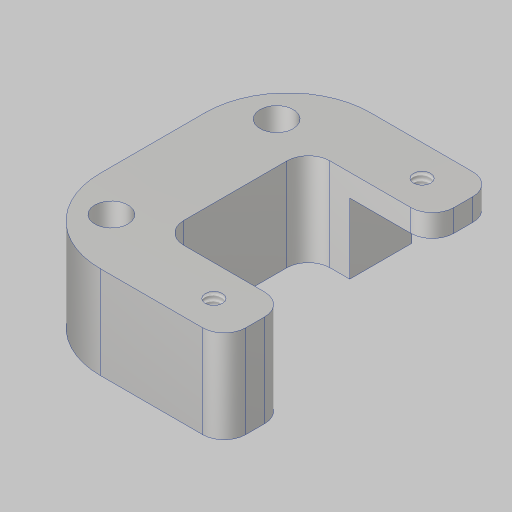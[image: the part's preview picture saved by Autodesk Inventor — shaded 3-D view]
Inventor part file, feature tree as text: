
AUTODESK INVENTOR PART (.ipt)
format: ipt  version: 2023.5 (Build 275446000, 446)  size: 196,096 bytes
history: native  units: in
note: dims shown in document units (in); Inventor stores cm internally (conversion verified against a paired STEP export)
features: sketch x6, extrude x4, projected_geometry x3, hole x2, fillet x2
ambient origin geometry x8: Origin, YZ Plane, XZ Plane, XY Plane, X Axis, Y Axis, Z Axis, Center Point
bodies: Solid1 (feature_tree)
feature tree (17):
  extrude  "Extrusion1"  Depth=1.2598in
  hole  "Hole1"  [1 undecoded]
  extrude  "Extrusion2"  Depth=0.25in
  extrude  "Extrusion3"  Depth=0.75in
  hole  "Hole3"  [1 undecoded]
  fillet  "Fillet1"  Radius=0.25in
  fillet  "Fillet2"  Radius=1.0in
  extrude  "Extrusion4"  Depth=0.5in
  sketch  "Sketch1"  dims[d1=1.2598in d2=0.31in]
  sketch  "Sketch2"  dims[d4=0.25in d5=0.375in]
  sketch  "Sketch4"  dims[d6=1.25in d7=0.0in d8=0.25in]
  sketch  "Sketch5"  dims[d9=0.104in d10=0.276in d11=0.375in d12=0.25in d13=0.5635in d14=1.0in d15=0.8108in d25=0.75in]
  sketch  "Sketch6"  dims[d26=1.5in d27=0.0in d28=1.5in d29=0.0in d30=0.25in d31=1.0in]
  sketch  "Sketch7"  dims[d32=0.201in d33=0.75in d34=0.375in d35=0.25in d36=0.5635in d37=1.0in d38=0.8108in d39=0.5in d40=0.13in d41=0.5in d42=0.425in d43=0.0in]
  projected_geometry  "Project Cut Edges1"
  projected_geometry  "Project Cut Edges2"
  projected_geometry  "Project Cut Edges3"
note: 2 required parameter values undecoded (feature->parameter linkage not recoverable at this tier; creation-order binding heuristic only, values carry confidence <= 0.55)
